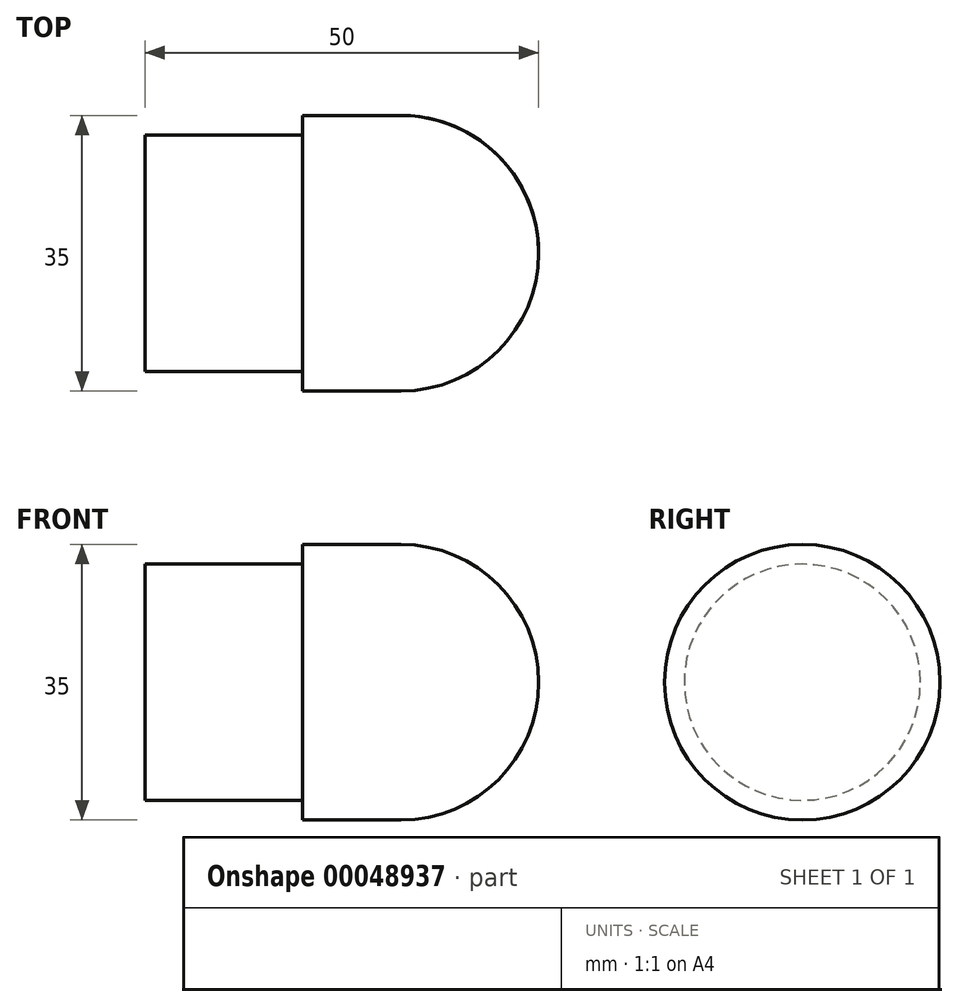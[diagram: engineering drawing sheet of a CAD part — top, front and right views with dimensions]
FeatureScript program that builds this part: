
annotation { "Feature Type Name" : "Feature", "Feature Type Description" : "" }
export const myFeature = defineFeature(function(context is Context, id is Id, definition is map)
    precondition{}
    {
        {
            var Q0;
            Q0=qCreatedBy(makeId("Top.planeOp"),FACE);
            var sketch = newSketch(context, id + "F0", { "sketchPlane" : qUnion([Q0])});
            skLineSegment(sketch, "E0", {"start": v(0, 0) * mm, "end": v(0, 15) * mm});
            skLineSegment(sketch, "E1", {"start": v(0, 15) * mm, "end": v(20, 15) * mm});
            skLineSegment(sketch, "E2", {"start": v(20, 15) * mm, "end": v(20, 17.5) * mm});
            skLineSegment(sketch, "E3", {"start": v(20, 17.5) * mm, "end": v(32.5, 17.5) * mm});
            skArc(sketch, "E4", {"start": v(32.5, 17.5) * mm, "mid": v(44.87, 12.37) * mm, "end": v(50, 0) * mm});
            skLineSegment(sketch, "E5", {"start": v(50, 0) * mm, "end": v(0, 0) * mm});
            skSolve(sketch);
        }
        {
            var Q0;
            Q0=makeQuery(id+"F0.imprint","IMPRINT",FACE,{"disambiguationData":[TD([[makeQuery(id+"F0.imprint","IMPRINT",EDGE,{"derivedFrom":sQuery(id+"F0.wireOp",EDGE,"E0")}),-1.0]])]});
            var Q1;
            Q1=sQuery(id+"F0.wireOp",EDGE,"E5");
            revolve(context, id + "F1", {"entities" : qUnion([Q0]), "axis" : qUnion([Q1]), "revolveType" : RevolveType.FULL});
        }
    });
